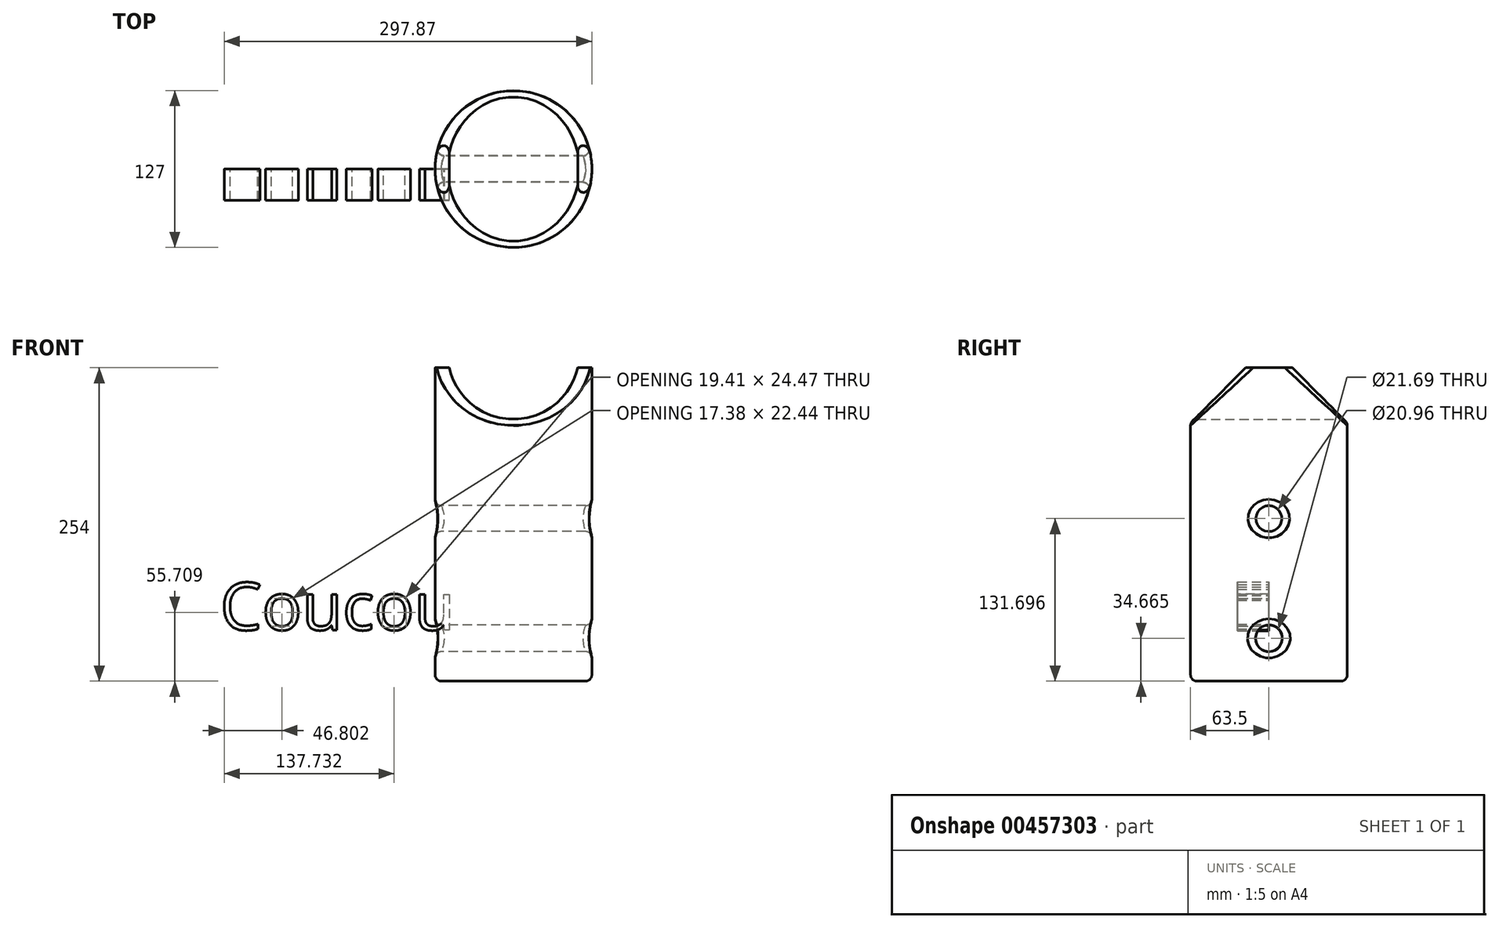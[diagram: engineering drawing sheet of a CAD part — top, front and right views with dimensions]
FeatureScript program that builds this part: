
annotation { "Feature Type Name" : "Feature", "Feature Type Description" : "" }
export const myFeature = defineFeature(function(context is Context, id is Id, definition is map)
    precondition{}
    {
        {
            var Q0;
            Q0=qCreatedBy(makeId("Top.planeOp"),FACE);
            var sketch = newSketch(context, id + "F0", { "sketchPlane" : qUnion([Q0])});
            skCircle(sketch, "E0", {"center": v(0, 0) * mm, "radius": 63.5 * mm});
            skSolve(sketch);
        }
        {
            var Q0;
            Q0=makeQuery(id+"F0.imprint","IMPRINT",FACE,{"disambiguationData":[TD([[makeQuery(id+"F0.imprint","IMPRINT",EDGE,{"derivedFrom":sQuery(id+"F0.wireOp",EDGE,"E0")}),1.0]])]});
            extrude(context, id + "F1", {"entities" : qUnion([Q0]), "depth" : 254 * mm});
        }
        {
            var Q0;
            Q0=qCreatedBy(makeId("Front.planeOp"),FACE);
            var sketch = newSketch(context, id + "F2", { "sketchPlane" : qUnion([Q0])});
            skCircle(sketch, "E1", {"center": v(0, 265.41) * mm, "radius": 53.25 * mm});
            skSolve(sketch);
        }
        {
            var Q0;
            Q0=makeQuery(id+"F2.imprint","IMPRINT",FACE,{"disambiguationData":[TD([[makeQuery(id+"F2.imprint","IMPRINT",EDGE,{"derivedFrom":sQuery(id+"F2.wireOp",EDGE,"E1")}),1.0]])]});
            extrude(context, id + "F3", {"entities" : qUnion([Q0]), "operationType" : NewBodyOperationType.REMOVE, "endBound" : BoundingType.SYMMETRIC, "depth" : 508 * mm});
        }
        {
            var Q0;
            Q0=qCreatedBy(makeId("Right.planeOp"),FACE);
            var sketch = newSketch(context, id + "F4", { "sketchPlane" : qUnion([Q0])});
            skCircle(sketch, "E2", {"center": v(0, 131.7) * mm, "radius": 10.48 * mm});
            skCircle(sketch, "E3", {"center": v(0, 34.66) * mm, "radius": 10.85 * mm});
            skSolve(sketch);
        }
        {
            var Q0;
            Q0 = qSketchRegion(id + "F4", true);
            extrude(context, id + "F5", {"entities" : qUnion([Q0]), "operationType" : NewBodyOperationType.REMOVE, "endBound" : BoundingType.SYMMETRIC, "depth" : 508 * mm});
        }
        {
            var Q0;
            Q0=makeQuery(id+"F3.boolean.opBoolean","INTERSECT",EDGE,{"disambiguationData":[OD(1.0)],"derivedFrom":[makeQuery(id+"F1.opExtrude","SWEPT_FACE",FACE,{"disambiguationData":[OSD([sQuery(id+"F0.wireOp",EDGE,"E0")])]}),makeQuery(id+"F3.opExtrude","SWEPT_FACE",FACE,{"disambiguationData":[OSD([sQuery(id+"F2.wireOp",EDGE,"E1")])]})]});
            var Q1;
            Q1=makeQuery(id+"F3.boolean.opBoolean","INTERSECT",EDGE,{"disambiguationData":[OD(0.0)],"derivedFrom":[makeQuery(id+"F1.opExtrude","SWEPT_FACE",FACE,{"disambiguationData":[OSD([sQuery(id+"F0.wireOp",EDGE,"E0")])]}),makeQuery(id+"F3.opExtrude","SWEPT_FACE",FACE,{"disambiguationData":[OSD([sQuery(id+"F2.wireOp",EDGE,"E1")])]})]});
            var Q2;
            Q2=makeQuery(id+"F5.boolean.opBoolean","INTERSECT",EDGE,{"disambiguationData":[OD(0.0)],"derivedFrom":[makeQuery(id+"F1.opExtrude","SWEPT_FACE",FACE,{"disambiguationData":[OSD([sQuery(id+"F0.wireOp",EDGE,"E0")])]}),makeQuery(id+"F5.opExtrude","SWEPT_FACE",FACE,{"disambiguationData":[OSD([sQuery(id+"F4.wireOp",EDGE,"E2")])]})]});
            var Q3;
            Q3=makeQuery(id+"F5.boolean.opBoolean","INTERSECT",EDGE,{"disambiguationData":[OD(0.0)],"derivedFrom":[makeQuery(id+"F1.opExtrude","SWEPT_FACE",FACE,{"disambiguationData":[OSD([sQuery(id+"F0.wireOp",EDGE,"E0")])]}),makeQuery(id+"F5.opExtrude","SWEPT_FACE",FACE,{"disambiguationData":[OSD([sQuery(id+"F4.wireOp",EDGE,"E3")])]})]});
            var Q4;
            Q4=makeQuery(id+"F1.opExtrude","CAP_EDGE",EDGE,{"disambiguationData":[OSD([sQuery(id+"F0.wireOp",EDGE,"E0")])],"isStart":true});
            var Q5;
            Q5=makeQuery(id+"F5.boolean.opBoolean","INTERSECT",EDGE,{"disambiguationData":[OD(1.0)],"derivedFrom":[makeQuery(id+"F1.opExtrude","SWEPT_FACE",FACE,{"disambiguationData":[OSD([sQuery(id+"F0.wireOp",EDGE,"E0")])]}),makeQuery(id+"F5.opExtrude","SWEPT_FACE",FACE,{"disambiguationData":[OSD([sQuery(id+"F4.wireOp",EDGE,"E2")])]})]});
            var Q6;
            Q6=makeQuery(id+"F5.boolean.opBoolean","INTERSECT",EDGE,{"disambiguationData":[OD(1.0)],"derivedFrom":[makeQuery(id+"F1.opExtrude","SWEPT_FACE",FACE,{"disambiguationData":[OSD([sQuery(id+"F0.wireOp",EDGE,"E0")])]}),makeQuery(id+"F5.opExtrude","SWEPT_FACE",FACE,{"disambiguationData":[OSD([sQuery(id+"F4.wireOp",EDGE,"E3")])]})]});
            fillet(context, id + "F6", {"entities" : qUnion([Q0, Q1, Q2, Q3, Q4, Q5, Q6]), "radius" : 5.08 * mm, "tangentPropagation" : true, "allowEdgeOverflow" : false});
        }
        {
            var Q0;
            Q0=qCreatedBy(makeId("Front.planeOp"),FACE);
            var sketch = newSketch(context, id + "F7", { "sketchPlane" : qUnion([Q0])});
            skText(sketch, "E4", { "text": "Coucou", "fontName": "OpenSans-Regular.ttf"});
            const initialGuessF7  = {"E4": [-0.23765, 0.04137, 1, 0, 0.03865]};
            skSetInitialGuess(sketch, initialGuessF7);
            skSolve(sketch);
        }
        {
            var Q0;
            Q0 = qSketchRegion(id + "F7", true);
            extrude(context, id + "F8", {"entities" : qUnion([Q0]), "depth" : 25.4 * mm});
        }
        {
            var Q0;
            Q0=makeQuery(id+"F8.opExtrude","CAP_EDGE",EDGE,{"disambiguationData":[OSD([sQuery(id+"F7.wireOp",EDGE,"E4.sketch_text.stroke-78")])],"isStart":false});
            var Q1;
            Q1=makeQuery(id+"F8.opExtrude","CAP_EDGE",EDGE,{"disambiguationData":[OSD([sQuery(id+"F7.wireOp",EDGE,"E4.sketch_text.stroke-77")])],"isStart":false});
            var Q2;
            Q2=makeQuery(id+"F8.opExtrude","CAP_FACE",FACE,{"disambiguationData":[OSD([sQuery(id+"F7.wireOp",EDGE,"E4.sketch_text.stroke-64"),sQuery(id+"F7.wireOp",EDGE,"E4.sketch_text.stroke-65"),sQuery(id+"F7.wireOp",EDGE,"E4.sketch_text.stroke-66"),sQuery(id+"F7.wireOp",EDGE,"E4.sketch_text.stroke-67"),sQuery(id+"F7.wireOp",EDGE,"E4.sketch_text.stroke-68"),sQuery(id+"F7.wireOp",EDGE,"E4.sketch_text.stroke-69"),sQuery(id+"F7.wireOp",EDGE,"E4.sketch_text.stroke-70"),sQuery(id+"F7.wireOp",EDGE,"E4.sketch_text.stroke-71"),sQuery(id+"F7.wireOp",EDGE,"E4.sketch_text.stroke-72"),sQuery(id+"F7.wireOp",EDGE,"E4.sketch_text.stroke-73"),sQuery(id+"F7.wireOp",EDGE,"E4.sketch_text.stroke-74"),sQuery(id+"F7.wireOp",EDGE,"E4.sketch_text.stroke-75"),sQuery(id+"F7.wireOp",EDGE,"E4.sketch_text.stroke-76"),sQuery(id+"F7.wireOp",EDGE,"E4.sketch_text.stroke-77"),sQuery(id+"F7.wireOp",EDGE,"E4.sketch_text.stroke-78"),sQuery(id+"F7.wireOp",EDGE,"E4.sketch_text.stroke-79"),sQuery(id+"F7.wireOp",EDGE,"E4.sketch_text.stroke-80")])],"isStart":false});
            var Q3;
            Q3=makeQuery(id+"F8.opExtrude","CAP_EDGE",EDGE,{"disambiguationData":[OSD([sQuery(id+"F7.wireOp",EDGE,"E4.sketch_text.stroke-75")])],"isStart":false});
            var Q4;
            Q4=makeQuery(id+"F8.opExtrude","CAP_EDGE",EDGE,{"disambiguationData":[OSD([sQuery(id+"F7.wireOp",EDGE,"E4.sketch_text.stroke-75")])],"isStart":true});
            var Q5;
            Q5=makeQuery(id+"F8.opExtrude","CAP_EDGE",EDGE,{"disambiguationData":[OSD([sQuery(id+"F7.wireOp",EDGE,"E4.sketch_text.stroke-74")])],"isStart":false});
            var Q6;
            Q6=makeQuery(id+"F8.opExtrude","CAP_EDGE",EDGE,{"disambiguationData":[OSD([sQuery(id+"F7.wireOp",EDGE,"E4.sketch_text.stroke-73")])],"isStart":false});
            var Q7;
            Q7=makeQuery(id+"F8.opExtrude","CAP_EDGE",EDGE,{"disambiguationData":[OSD([sQuery(id+"F7.wireOp",EDGE,"E4.sketch_text.stroke-80")])],"isStart":false});
            fillet(context, id + "F9", {"entities" : qUnion([Q0, Q1, Q2, Q3, Q4, Q5, Q6, Q7]), "radius" : 1.02 * mm, "tangentPropagation" : true, "allowEdgeOverflow" : false});
        }
    });
